# Revit family: Bath-Drop_In-Whirlpool-Heater-KOHLER-Riverbath-K-1360
name_source: partatom
category: Plumbing Fixtures
units: mm (PartAtom-declared; Revit-internal decimal feet)

## family parameters
Cut with Voids When Loaded = No
Host = Face
OmniClass Number = 23.31.15.00
OmniClass Title = Bathtubs
Part Type = Normal
Room Calculation Point = No
Round Connector Dimension = Use Diameter
Shared = No

## types (2) — shared parameters
ADA Compliant = No
Amplifer Electrical Connector = Amplifer Electrical Connector
Apparent Load = 4080 VA
Assembly Code = D2010500
Blower Electrical Connector = Blower Electrical Connector
CW Connection = Yes
Cold Water Inlet = Cold Water Inlet
Date Modified = 09/14/2023
Default Elevation = 0"
Description = 75 Inch x 45 Inch drop-in heated whirlpool bath
Drain Included = No
Electrical Connector = Yes
Electrical Note = Two Dedicated Circuit Required
HW Connection = Yes
Heater Electrical Connector = Heater Electrical Connector
Height = 25"
Hot Water Inlet = Hot Water Inlet
Length = 75"
Manufacturer = Kohler Co.
Master Format 2014 = 22 41 19
Master Format 2014 Name = Residential Bathtubs
Material = Acrylic
Pressure = 60.00 psi
Product Documentation Link = https://www.us.kohler.com
Product Name = Riverbath
Product Page URL = http://www.us.kohler.com
Pump Electrical Connector = Pump Electrical Connector
URL = https://www.us.kohler.com
Vent Connection = No
Voltage = 240 V
Waste Connection = Yes
Waste Water Outlet = Waste Water Outlet
WaterSense Certified = No
Width = 45"

## per-type parameters (varying)
| type | Finish | Model | Type |
| 0-White | KOHLER-Acrylic-0-White | K-1360-H2-0 | 1 |
| 47-Almond | KOHLER-Acrylic-47-Almond | K-1360-H2-47 | 2 |

## geometry (parser evidence)
native form markers: Sweep x6
no freeform markers — native parametric forms only
